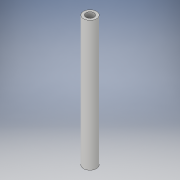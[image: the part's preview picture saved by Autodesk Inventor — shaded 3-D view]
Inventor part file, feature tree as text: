
AUTODESK INVENTOR PART (.ipt)
format: ipt  version: 2019.4 (Build 234330000, 330)  size: 93,184 bytes
history: native  units: in
note: dims shown in document units (in); Inventor stores cm internally (conversion verified against a paired STEP export)
features: extrude x1, sketch x1
ambient origin geometry x8: Origin, YZ Plane, XZ Plane, XY Plane, X Axis, Y Axis, Z Axis, Center Point
bodies: Solid1 (feature_tree)
feature tree (2):
  extrude  "Extrusion1"  Depth=3.1496in
  sketch  "Sketch1"  dims[d0=0.315in d1=0.1969in d2=3.1496in d3=0.0in]
